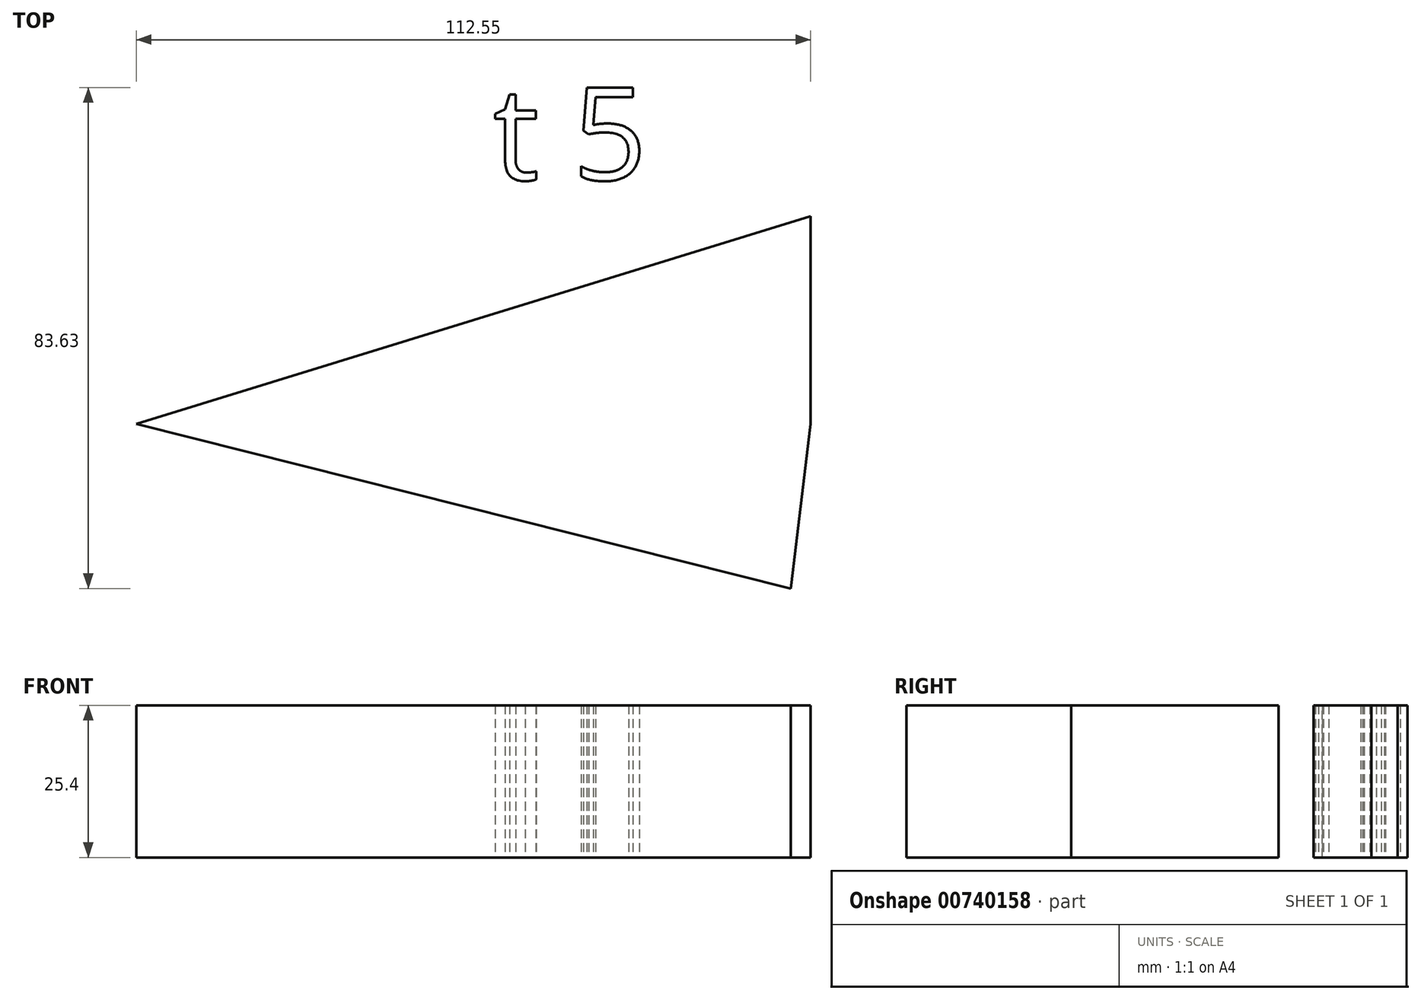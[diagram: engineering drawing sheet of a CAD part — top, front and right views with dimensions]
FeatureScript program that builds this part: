
annotation { "Feature Type Name" : "Feature", "Feature Type Description" : "" }
export const myFeature = defineFeature(function(context is Context, id is Id, definition is map)
    precondition{}
    {
        {
            var Q0;
            Q0=qCreatedBy(makeId("Top.planeOp"),FACE);
            var sketch = newSketch(context, id + "F0", { "sketchPlane" : qUnion([Q0])});
            skLineSegment(sketch, "E0", {"start": v(112.55, 0) * mm, "end": v(112.55, 34.65) * mm});
            skLineSegment(sketch, "E1", {"start": v(112.55, 34.65) * mm, "end": v(0, 0) * mm});
            skLineSegment(sketch, "E2", {"start": v(0, 0) * mm, "end": v(109.27, -27.48) * mm});
            skLineSegment(sketch, "E3", {"start": v(109.27, -27.48) * mm, "end": v(112.55, 0) * mm});
            skText(sketch, "E4", { "text": "t 5", "fontName": "OpenSans-Regular.ttf"});
            skFitSpline(sketch, "E5", {"points": [v(-50.4, 48.4) * mm, v(33.6, 77.59) * mm, v(13.01, 65.62) * mm], "startDerivative": vector(189.36, 70.46) * mm, "endDerivative": vector(-92.38, -48.63) * mm});
            const initialGuessF0  = {"E4": [0.05958, 0.0407, 1, 0, 0.01558]};
            skSetInitialGuess(sketch, initialGuessF0);
            skSolve(sketch);
        }
        {
            var Q0;
            Q0 = qSketchRegion(id + "F0", true);
            extrude(context, id + "F1", {"entities" : qUnion([Q0]), "depth" : 25.4 * mm, "offsetDistance" : 25.4 * mm});
        }
    });
